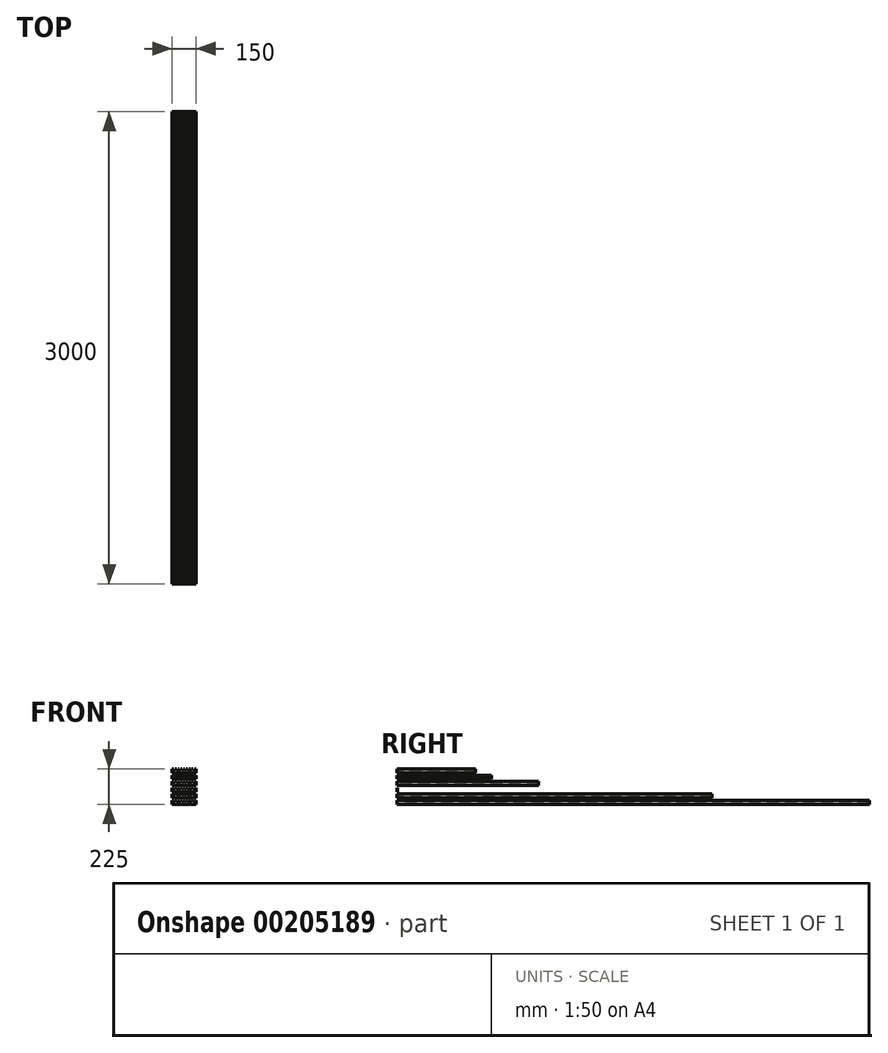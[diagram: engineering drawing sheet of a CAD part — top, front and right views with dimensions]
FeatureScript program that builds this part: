
annotation { "Feature Type Name" : "Feature", "Feature Type Description" : "" }
export const myFeature = defineFeature(function(context is Context, id is Id, definition is map)
    precondition{}
    {
        {
            var Q0;
            Q0=qCreatedBy(makeId("Front.planeOp"),FACE);
            var sketch = newSketch(context, id + "F0", { "sketchPlane" : qUnion([Q0])});
            skLineSegment(sketch, "E0.bottom", {"start": v(0, 0) * mm, "end": v(-150, 0) * mm});
            skLineSegment(sketch, "E0.top", {"start": v(0, 25) * mm, "end": v(-8.82, 25) * mm});
            skLineSegment(sketch, "E0.left", {"start": v(0, 0) * mm, "end": v(0, 25) * mm});
            skLineSegment(sketch, "E0.right", {"start": v(-150, 0) * mm, "end": v(-150, 25) * mm});
            skLineSegment(sketch, "E1", {"start": v(-141.18, 25) * mm, "end": v(-150, 25) * mm});
            skLineSegment(sketch, "E2", {"start": v(-132.35, 25) * mm, "end": v(-141.18, 25) * mm});
            skLineSegment(sketch, "E3", {"start": v(-123.53, 25) * mm, "end": v(-132.35, 25) * mm});
            skLineSegment(sketch, "E4", {"start": v(-114.7, 25) * mm, "end": v(-123.53, 25) * mm});
            skLineSegment(sketch, "E5", {"start": v(-105.88, 25) * mm, "end": v(-114.7, 25) * mm});
            skLineSegment(sketch, "E6", {"start": v(-97.06, 25) * mm, "end": v(-105.88, 25) * mm});
            skLineSegment(sketch, "E7", {"start": v(-88.24, 25) * mm, "end": v(-97.06, 25) * mm});
            skLineSegment(sketch, "E8", {"start": v(-79.41, 25) * mm, "end": v(-88.24, 25) * mm});
            skLineSegment(sketch, "E9", {"start": v(-70.59, 25) * mm, "end": v(-79.41, 25) * mm});
            skLineSegment(sketch, "E10", {"start": v(-61.76, 25) * mm, "end": v(-70.59, 25) * mm});
            skLineSegment(sketch, "E11", {"start": v(-52.94, 25) * mm, "end": v(-61.76, 25) * mm});
            skLineSegment(sketch, "E12", {"start": v(-44.12, 25) * mm, "end": v(-52.94, 25) * mm});
            skLineSegment(sketch, "E13", {"start": v(-35.3, 25) * mm, "end": v(-44.12, 25) * mm});
            skLineSegment(sketch, "E14", {"start": v(-26.47, 25) * mm, "end": v(-35.3, 25) * mm});
            skLineSegment(sketch, "E15", {"start": v(-17.65, 25) * mm, "end": v(-26.47, 25) * mm});
            skLineSegment(sketch, "E16", {"start": v(-8.82, 25) * mm, "end": v(-17.65, 25) * mm});
            skLineSegment(sketch, "E17.bottom", {"start": v(-141.18, 25) * mm, "end": v(-132.35, 25) * mm});
            skLineSegment(sketch, "E17.top", {"start": v(-141.18, 16.18) * mm, "end": v(-132.35, 16.18) * mm});
            skLineSegment(sketch, "E17.left", {"start": v(-141.18, 25) * mm, "end": v(-141.18, 16.18) * mm});
            skLineSegment(sketch, "E17.right", {"start": v(-132.35, 25) * mm, "end": v(-132.35, 16.18) * mm});
            skLineSegment(sketch, "E18.bottom", {"start": v(-123.53, 25) * mm, "end": v(-114.7, 25) * mm});
            skLineSegment(sketch, "E18.top", {"start": v(-123.53, 16.18) * mm, "end": v(-114.7, 16.18) * mm});
            skLineSegment(sketch, "E18.left", {"start": v(-123.53, 25) * mm, "end": v(-123.53, 16.18) * mm});
            skLineSegment(sketch, "E18.right", {"start": v(-114.7, 25) * mm, "end": v(-114.7, 16.18) * mm});
            skLineSegment(sketch, "E19.bottom", {"start": v(-105.88, 25) * mm, "end": v(-97.06, 25) * mm});
            skLineSegment(sketch, "E19.top", {"start": v(-105.88, 16.18) * mm, "end": v(-97.06, 16.18) * mm});
            skLineSegment(sketch, "E19.left", {"start": v(-105.88, 25) * mm, "end": v(-105.88, 16.18) * mm});
            skLineSegment(sketch, "E19.right", {"start": v(-97.06, 25) * mm, "end": v(-97.06, 16.18) * mm});
            skLineSegment(sketch, "E20.bottom", {"start": v(-88.24, 25) * mm, "end": v(-79.41, 25) * mm});
            skLineSegment(sketch, "E20.top", {"start": v(-88.24, 16.18) * mm, "end": v(-79.41, 16.18) * mm});
            skLineSegment(sketch, "E20.left", {"start": v(-88.24, 25) * mm, "end": v(-88.24, 16.18) * mm});
            skLineSegment(sketch, "E20.right", {"start": v(-79.41, 25) * mm, "end": v(-79.41, 16.18) * mm});
            skLineSegment(sketch, "E21.bottom", {"start": v(-70.59, 25) * mm, "end": v(-61.76, 25) * mm});
            skLineSegment(sketch, "E21.top", {"start": v(-70.59, 16.18) * mm, "end": v(-61.76, 16.18) * mm});
            skLineSegment(sketch, "E21.left", {"start": v(-70.59, 25) * mm, "end": v(-70.59, 16.18) * mm});
            skLineSegment(sketch, "E21.right", {"start": v(-61.76, 25) * mm, "end": v(-61.76, 16.18) * mm});
            skLineSegment(sketch, "E22.bottom", {"start": v(-52.94, 25) * mm, "end": v(-44.12, 25) * mm});
            skLineSegment(sketch, "E22.top", {"start": v(-52.94, 16.18) * mm, "end": v(-44.12, 16.18) * mm});
            skLineSegment(sketch, "E22.left", {"start": v(-52.94, 25) * mm, "end": v(-52.94, 16.18) * mm});
            skLineSegment(sketch, "E22.right", {"start": v(-44.12, 25) * mm, "end": v(-44.12, 16.18) * mm});
            skLineSegment(sketch, "E23.bottom", {"start": v(-35.3, 25) * mm, "end": v(-26.47, 25) * mm});
            skLineSegment(sketch, "E23.top", {"start": v(-35.3, 16.18) * mm, "end": v(-26.47, 16.18) * mm});
            skLineSegment(sketch, "E23.left", {"start": v(-35.3, 25) * mm, "end": v(-35.3, 16.18) * mm});
            skLineSegment(sketch, "E23.right", {"start": v(-26.47, 25) * mm, "end": v(-26.47, 16.18) * mm});
            skLineSegment(sketch, "E24.bottom", {"start": v(-17.65, 25) * mm, "end": v(-8.82, 25) * mm});
            skLineSegment(sketch, "E24.top", {"start": v(-17.65, 16.18) * mm, "end": v(-8.82, 16.18) * mm});
            skLineSegment(sketch, "E24.left", {"start": v(-17.65, 25) * mm, "end": v(-17.65, 16.18) * mm});
            skLineSegment(sketch, "E24.right", {"start": v(-8.82, 25) * mm, "end": v(-8.82, 16.18) * mm});
            skLineSegment(sketch, "E25.bottom", {"start": v(-114.7, 0) * mm, "end": v(-110.7, 0) * mm});
            skLineSegment(sketch, "E25.top", {"start": v(-114.7, 4) * mm, "end": v(-110.7, 4) * mm});
            skLineSegment(sketch, "E25.left", {"start": v(-114.7, 0) * mm, "end": v(-114.7, 4) * mm});
            skLineSegment(sketch, "E25.right", {"start": v(-110.7, 0) * mm, "end": v(-110.7, 4) * mm});
            skLineSegment(sketch, "E26.bottom", {"start": v(-35.3, 0) * mm, "end": v(-39.3, 0) * mm});
            skLineSegment(sketch, "E26.top", {"start": v(-35.3, 4) * mm, "end": v(-39.3, 4) * mm});
            skLineSegment(sketch, "E26.left", {"start": v(-35.3, 0) * mm, "end": v(-35.3, 4) * mm});
            skLineSegment(sketch, "E26.right", {"start": v(-39.3, 0) * mm, "end": v(-39.3, 4) * mm});
            skLineSegment(sketch, "E27.0.1.0", {"start": v(-35.3, 65) * mm, "end": v(-44.12, 65) * mm});
            skLineSegment(sketch, "E27.0.1.1", {"start": v(-17.65, 56.18) * mm, "end": v(-8.82, 56.18) * mm});
            skLineSegment(sketch, "E27.0.1.2", {"start": v(-17.65, 65) * mm, "end": v(-17.65, 56.18) * mm});
            skLineSegment(sketch, "E27.0.1.3", {"start": v(-123.53, 65) * mm, "end": v(-114.7, 65) * mm});
            skLineSegment(sketch, "E27.0.1.4", {"start": v(-132.35, 65) * mm, "end": v(-132.35, 56.18) * mm});
            skLineSegment(sketch, "E27.0.1.5", {"start": v(-150, 40) * mm, "end": v(-150, 65) * mm});
            skLineSegment(sketch, "E27.0.1.6", {"start": v(0, 40) * mm, "end": v(0, 65) * mm});
            skLineSegment(sketch, "E27.0.1.7", {"start": v(-17.65, 65) * mm, "end": v(-8.82, 65) * mm});
            skLineSegment(sketch, "E27.0.1.8", {"start": v(-88.24, 65) * mm, "end": v(-97.06, 65) * mm});
            skLineSegment(sketch, "E27.0.1.9", {"start": v(-141.18, 65) * mm, "end": v(-150, 65) * mm});
            skLineSegment(sketch, "E27.0.1.10", {"start": v(-123.53, 56.18) * mm, "end": v(-114.7, 56.18) * mm});
            skLineSegment(sketch, "E27.0.1.11", {"start": v(0, 40) * mm, "end": v(-150, 40) * mm});
            skLineSegment(sketch, "E27.0.1.12", {"start": v(-61.76, 65) * mm, "end": v(-61.76, 56.18) * mm});
            skLineSegment(sketch, "E27.0.1.13", {"start": v(-88.24, 65) * mm, "end": v(-88.24, 56.18) * mm});
            skLineSegment(sketch, "E27.0.1.14", {"start": v(-61.76, 65) * mm, "end": v(-70.59, 65) * mm});
            skLineSegment(sketch, "E27.0.1.15", {"start": v(-70.59, 65) * mm, "end": v(-70.59, 56.18) * mm});
            skLineSegment(sketch, "E27.0.1.16", {"start": v(-97.06, 65) * mm, "end": v(-97.06, 56.18) * mm});
            skLineSegment(sketch, "E27.0.1.17", {"start": v(-26.47, 65) * mm, "end": v(-26.47, 56.18) * mm});
            skLineSegment(sketch, "E27.0.1.18", {"start": v(-141.18, 65) * mm, "end": v(-141.18, 56.18) * mm});
            skLineSegment(sketch, "E27.0.1.19", {"start": v(-105.88, 65) * mm, "end": v(-105.88, 56.18) * mm});
            skLineSegment(sketch, "E27.0.1.20", {"start": v(-70.59, 56.18) * mm, "end": v(-61.76, 56.18) * mm});
            skLineSegment(sketch, "E27.0.1.21", {"start": v(-35.3, 65) * mm, "end": v(-35.3, 56.18) * mm});
            skLineSegment(sketch, "E27.0.1.22", {"start": v(-114.7, 65) * mm, "end": v(-114.7, 56.18) * mm});
            skLineSegment(sketch, "E27.0.1.23", {"start": v(-44.12, 65) * mm, "end": v(-44.12, 56.18) * mm});
            skLineSegment(sketch, "E27.0.1.24", {"start": v(-79.41, 65) * mm, "end": v(-79.41, 56.18) * mm});
            skLineSegment(sketch, "E27.0.1.25", {"start": v(-8.82, 65) * mm, "end": v(-8.82, 56.18) * mm});
            skLineSegment(sketch, "E27.0.1.26", {"start": v(-123.53, 65) * mm, "end": v(-123.53, 56.18) * mm});
            skLineSegment(sketch, "E27.0.1.27", {"start": v(-52.94, 65) * mm, "end": v(-52.94, 56.18) * mm});
            skLineSegment(sketch, "E27.0.1.28", {"start": v(-114.7, 65) * mm, "end": v(-123.53, 65) * mm});
            skLineSegment(sketch, "E27.0.1.29", {"start": v(-70.59, 65) * mm, "end": v(-61.76, 65) * mm});
            skLineSegment(sketch, "E27.0.1.30", {"start": v(-8.82, 65) * mm, "end": v(-17.65, 65) * mm});
            skLineSegment(sketch, "E27.0.1.31", {"start": v(-88.24, 56.18) * mm, "end": v(-79.41, 56.18) * mm});
            skLineSegment(sketch, "E27.0.1.32", {"start": v(-35.3, 40) * mm, "end": v(-39.3, 40) * mm});
            skLineSegment(sketch, "E27.0.1.33", {"start": v(0, 65) * mm, "end": v(-8.82, 65) * mm});
            skLineSegment(sketch, "E27.0.1.34", {"start": v(-35.3, 44) * mm, "end": v(-39.3, 44) * mm});
            skLineSegment(sketch, "E27.0.1.35", {"start": v(-52.94, 56.18) * mm, "end": v(-44.12, 56.18) * mm});
            skLineSegment(sketch, "E27.0.1.36", {"start": v(-110.7, 40) * mm, "end": v(-110.7, 44) * mm});
            skLineSegment(sketch, "E27.0.1.37", {"start": v(-114.7, 40) * mm, "end": v(-114.7, 44) * mm});
            skLineSegment(sketch, "E27.0.1.38", {"start": v(-114.7, 44) * mm, "end": v(-110.7, 44) * mm});
            skLineSegment(sketch, "E27.0.1.39", {"start": v(-141.18, 56.18) * mm, "end": v(-132.35, 56.18) * mm});
            skLineSegment(sketch, "E27.0.1.40", {"start": v(-105.88, 56.18) * mm, "end": v(-97.06, 56.18) * mm});
            skLineSegment(sketch, "E27.0.1.41", {"start": v(-114.7, 40) * mm, "end": v(-110.7, 40) * mm});
            skLineSegment(sketch, "E27.0.1.42", {"start": v(-35.3, 56.18) * mm, "end": v(-26.47, 56.18) * mm});
            skLineSegment(sketch, "E27.0.1.43", {"start": v(-39.3, 40) * mm, "end": v(-39.3, 44) * mm});
            skLineSegment(sketch, "E27.0.1.44", {"start": v(-35.3, 40) * mm, "end": v(-35.3, 44) * mm});
            skLineSegment(sketch, "E27.0.1.45", {"start": v(-105.88, 65) * mm, "end": v(-114.7, 65) * mm});
            skLineSegment(sketch, "E27.0.1.46", {"start": v(-123.53, 65) * mm, "end": v(-132.35, 65) * mm});
            skLineSegment(sketch, "E27.0.1.47", {"start": v(-26.47, 65) * mm, "end": v(-35.3, 65) * mm});
            skLineSegment(sketch, "E27.0.1.48", {"start": v(-88.24, 65) * mm, "end": v(-79.41, 65) * mm});
            skLineSegment(sketch, "E27.0.1.49", {"start": v(-52.94, 65) * mm, "end": v(-44.12, 65) * mm});
            skLineSegment(sketch, "E27.0.1.50", {"start": v(-17.65, 65) * mm, "end": v(-26.47, 65) * mm});
            skLineSegment(sketch, "E27.0.1.51", {"start": v(-132.35, 65) * mm, "end": v(-141.18, 65) * mm});
            skLineSegment(sketch, "E27.0.1.52", {"start": v(-97.06, 65) * mm, "end": v(-105.88, 65) * mm});
            skLineSegment(sketch, "E27.0.1.53", {"start": v(-70.59, 65) * mm, "end": v(-79.41, 65) * mm});
            skLineSegment(sketch, "E27.0.1.54", {"start": v(-52.94, 65) * mm, "end": v(-61.76, 65) * mm});
            skLineSegment(sketch, "E27.0.1.55", {"start": v(-79.41, 65) * mm, "end": v(-88.24, 65) * mm});
            skLineSegment(sketch, "E27.0.1.56", {"start": v(-44.12, 65) * mm, "end": v(-52.94, 65) * mm});
            skLineSegment(sketch, "E27.0.1.57", {"start": v(-105.88, 65) * mm, "end": v(-97.06, 65) * mm});
            skLineSegment(sketch, "E27.0.1.58", {"start": v(-35.3, 65) * mm, "end": v(-26.47, 65) * mm});
            skLineSegment(sketch, "E27.0.1.59", {"start": v(-141.18, 65) * mm, "end": v(-132.35, 65) * mm});
            skLineSegment(sketch, "E27.0.2.0", {"start": v(-35.3, 105) * mm, "end": v(-44.12, 105) * mm});
            skLineSegment(sketch, "E27.0.2.1", {"start": v(-17.65, 96.18) * mm, "end": v(-8.82, 96.18) * mm});
            skLineSegment(sketch, "E27.0.2.2", {"start": v(-17.65, 105) * mm, "end": v(-17.65, 96.18) * mm});
            skLineSegment(sketch, "E27.0.2.3", {"start": v(-123.53, 105) * mm, "end": v(-114.7, 105) * mm});
            skLineSegment(sketch, "E27.0.2.4", {"start": v(-132.35, 105) * mm, "end": v(-132.35, 96.18) * mm});
            skLineSegment(sketch, "E27.0.2.5", {"start": v(-150, 80) * mm, "end": v(-150, 105) * mm});
            skLineSegment(sketch, "E27.0.2.6", {"start": v(0, 80) * mm, "end": v(0, 105) * mm});
            skLineSegment(sketch, "E27.0.2.7", {"start": v(-17.65, 105) * mm, "end": v(-8.82, 105) * mm});
            skLineSegment(sketch, "E27.0.2.8", {"start": v(-88.24, 105) * mm, "end": v(-97.06, 105) * mm});
            skLineSegment(sketch, "E27.0.2.9", {"start": v(-141.18, 105) * mm, "end": v(-150, 105) * mm});
            skLineSegment(sketch, "E27.0.2.10", {"start": v(-123.53, 96.18) * mm, "end": v(-114.7, 96.18) * mm});
            skLineSegment(sketch, "E27.0.2.11", {"start": v(0, 80) * mm, "end": v(-150, 80) * mm});
            skLineSegment(sketch, "E27.0.2.12", {"start": v(-61.76, 105) * mm, "end": v(-61.76, 96.18) * mm});
            skLineSegment(sketch, "E27.0.2.13", {"start": v(-88.24, 105) * mm, "end": v(-88.24, 96.18) * mm});
            skLineSegment(sketch, "E27.0.2.14", {"start": v(-61.76, 105) * mm, "end": v(-70.59, 105) * mm});
            skLineSegment(sketch, "E27.0.2.15", {"start": v(-70.59, 105) * mm, "end": v(-70.59, 96.18) * mm});
            skLineSegment(sketch, "E27.0.2.16", {"start": v(-97.06, 105) * mm, "end": v(-97.06, 96.18) * mm});
            skLineSegment(sketch, "E27.0.2.17", {"start": v(-26.47, 105) * mm, "end": v(-26.47, 96.18) * mm});
            skLineSegment(sketch, "E27.0.2.18", {"start": v(-141.18, 105) * mm, "end": v(-141.18, 96.18) * mm});
            skLineSegment(sketch, "E27.0.2.19", {"start": v(-105.88, 105) * mm, "end": v(-105.88, 96.18) * mm});
            skLineSegment(sketch, "E27.0.2.20", {"start": v(-70.59, 96.18) * mm, "end": v(-61.76, 96.18) * mm});
            skLineSegment(sketch, "E27.0.2.21", {"start": v(-35.3, 105) * mm, "end": v(-35.3, 96.18) * mm});
            skLineSegment(sketch, "E27.0.2.22", {"start": v(-114.7, 105) * mm, "end": v(-114.7, 96.18) * mm});
            skLineSegment(sketch, "E27.0.2.23", {"start": v(-44.12, 105) * mm, "end": v(-44.12, 96.18) * mm});
            skLineSegment(sketch, "E27.0.2.24", {"start": v(-79.41, 105) * mm, "end": v(-79.41, 96.18) * mm});
            skLineSegment(sketch, "E27.0.2.25", {"start": v(-8.82, 105) * mm, "end": v(-8.82, 96.18) * mm});
            skLineSegment(sketch, "E27.0.2.26", {"start": v(-123.53, 105) * mm, "end": v(-123.53, 96.18) * mm});
            skLineSegment(sketch, "E27.0.2.27", {"start": v(-52.94, 105) * mm, "end": v(-52.94, 96.18) * mm});
            skLineSegment(sketch, "E27.0.2.28", {"start": v(-114.7, 105) * mm, "end": v(-123.53, 105) * mm});
            skLineSegment(sketch, "E27.0.2.29", {"start": v(-70.59, 105) * mm, "end": v(-61.76, 105) * mm});
            skLineSegment(sketch, "E27.0.2.30", {"start": v(-8.82, 105) * mm, "end": v(-17.65, 105) * mm});
            skLineSegment(sketch, "E27.0.2.31", {"start": v(-88.24, 96.18) * mm, "end": v(-79.41, 96.18) * mm});
            skLineSegment(sketch, "E27.0.2.32", {"start": v(-35.3, 80) * mm, "end": v(-39.3, 80) * mm});
            skLineSegment(sketch, "E27.0.2.33", {"start": v(0, 105) * mm, "end": v(-8.82, 105) * mm});
            skLineSegment(sketch, "E27.0.2.34", {"start": v(-35.3, 84) * mm, "end": v(-39.3, 84) * mm});
            skLineSegment(sketch, "E27.0.2.35", {"start": v(-52.94, 96.18) * mm, "end": v(-44.12, 96.18) * mm});
            skLineSegment(sketch, "E27.0.2.36", {"start": v(-110.7, 80) * mm, "end": v(-110.7, 84) * mm});
            skLineSegment(sketch, "E27.0.2.37", {"start": v(-114.7, 80) * mm, "end": v(-114.7, 84) * mm});
            skLineSegment(sketch, "E27.0.2.38", {"start": v(-114.7, 84) * mm, "end": v(-110.7, 84) * mm});
            skLineSegment(sketch, "E27.0.2.39", {"start": v(-141.18, 96.18) * mm, "end": v(-132.35, 96.18) * mm});
            skLineSegment(sketch, "E27.0.2.40", {"start": v(-105.88, 96.18) * mm, "end": v(-97.06, 96.18) * mm});
            skLineSegment(sketch, "E27.0.2.41", {"start": v(-114.7, 80) * mm, "end": v(-110.7, 80) * mm});
            skLineSegment(sketch, "E27.0.2.42", {"start": v(-35.3, 96.18) * mm, "end": v(-26.47, 96.18) * mm});
            skLineSegment(sketch, "E27.0.2.43", {"start": v(-39.3, 80) * mm, "end": v(-39.3, 84) * mm});
            skLineSegment(sketch, "E27.0.2.44", {"start": v(-35.3, 80) * mm, "end": v(-35.3, 84) * mm});
            skLineSegment(sketch, "E27.0.2.45", {"start": v(-105.88, 105) * mm, "end": v(-114.7, 105) * mm});
            skLineSegment(sketch, "E27.0.2.46", {"start": v(-123.53, 105) * mm, "end": v(-132.35, 105) * mm});
            skLineSegment(sketch, "E27.0.2.47", {"start": v(-26.47, 105) * mm, "end": v(-35.3, 105) * mm});
            skLineSegment(sketch, "E27.0.2.48", {"start": v(-88.24, 105) * mm, "end": v(-79.41, 105) * mm});
            skLineSegment(sketch, "E27.0.2.49", {"start": v(-52.94, 105) * mm, "end": v(-44.12, 105) * mm});
            skLineSegment(sketch, "E27.0.2.50", {"start": v(-17.65, 105) * mm, "end": v(-26.47, 105) * mm});
            skLineSegment(sketch, "E27.0.2.51", {"start": v(-132.35, 105) * mm, "end": v(-141.18, 105) * mm});
            skLineSegment(sketch, "E27.0.2.52", {"start": v(-97.06, 105) * mm, "end": v(-105.88, 105) * mm});
            skLineSegment(sketch, "E27.0.2.53", {"start": v(-70.59, 105) * mm, "end": v(-79.41, 105) * mm});
            skLineSegment(sketch, "E27.0.2.54", {"start": v(-52.94, 105) * mm, "end": v(-61.76, 105) * mm});
            skLineSegment(sketch, "E27.0.2.55", {"start": v(-79.41, 105) * mm, "end": v(-88.24, 105) * mm});
            skLineSegment(sketch, "E27.0.2.56", {"start": v(-44.12, 105) * mm, "end": v(-52.94, 105) * mm});
            skLineSegment(sketch, "E27.0.2.57", {"start": v(-105.88, 105) * mm, "end": v(-97.06, 105) * mm});
            skLineSegment(sketch, "E27.0.2.58", {"start": v(-35.3, 105) * mm, "end": v(-26.47, 105) * mm});
            skLineSegment(sketch, "E27.0.2.59", {"start": v(-141.18, 105) * mm, "end": v(-132.35, 105) * mm});
            skLineSegment(sketch, "E27.0.3.0", {"start": v(-35.3, 145) * mm, "end": v(-44.12, 145) * mm});
            skLineSegment(sketch, "E27.0.3.1", {"start": v(-17.65, 136.18) * mm, "end": v(-8.82, 136.18) * mm});
            skLineSegment(sketch, "E27.0.3.2", {"start": v(-17.65, 145) * mm, "end": v(-17.65, 136.18) * mm});
            skLineSegment(sketch, "E27.0.3.3", {"start": v(-123.53, 145) * mm, "end": v(-114.7, 145) * mm});
            skLineSegment(sketch, "E27.0.3.4", {"start": v(-132.35, 145) * mm, "end": v(-132.35, 136.18) * mm});
            skLineSegment(sketch, "E27.0.3.5", {"start": v(-150, 120) * mm, "end": v(-150, 145) * mm});
            skLineSegment(sketch, "E27.0.3.6", {"start": v(0, 120) * mm, "end": v(0, 145) * mm});
            skLineSegment(sketch, "E27.0.3.7", {"start": v(-17.65, 145) * mm, "end": v(-8.82, 145) * mm});
            skLineSegment(sketch, "E27.0.3.8", {"start": v(-88.24, 145) * mm, "end": v(-97.06, 145) * mm});
            skLineSegment(sketch, "E27.0.3.9", {"start": v(-141.18, 145) * mm, "end": v(-150, 145) * mm});
            skLineSegment(sketch, "E27.0.3.10", {"start": v(-123.53, 136.18) * mm, "end": v(-114.7, 136.18) * mm});
            skLineSegment(sketch, "E27.0.3.11", {"start": v(0, 120) * mm, "end": v(-150, 120) * mm});
            skLineSegment(sketch, "E27.0.3.12", {"start": v(-61.76, 145) * mm, "end": v(-61.76, 136.18) * mm});
            skLineSegment(sketch, "E27.0.3.13", {"start": v(-88.24, 145) * mm, "end": v(-88.24, 136.18) * mm});
            skLineSegment(sketch, "E27.0.3.14", {"start": v(-61.76, 145) * mm, "end": v(-70.59, 145) * mm});
            skLineSegment(sketch, "E27.0.3.15", {"start": v(-70.59, 145) * mm, "end": v(-70.59, 136.18) * mm});
            skLineSegment(sketch, "E27.0.3.16", {"start": v(-97.06, 145) * mm, "end": v(-97.06, 136.18) * mm});
            skLineSegment(sketch, "E27.0.3.17", {"start": v(-26.47, 145) * mm, "end": v(-26.47, 136.18) * mm});
            skLineSegment(sketch, "E27.0.3.18", {"start": v(-141.18, 145) * mm, "end": v(-141.18, 136.18) * mm});
            skLineSegment(sketch, "E27.0.3.19", {"start": v(-105.88, 145) * mm, "end": v(-105.88, 136.18) * mm});
            skLineSegment(sketch, "E27.0.3.20", {"start": v(-70.59, 136.18) * mm, "end": v(-61.76, 136.18) * mm});
            skLineSegment(sketch, "E27.0.3.21", {"start": v(-35.3, 145) * mm, "end": v(-35.3, 136.18) * mm});
            skLineSegment(sketch, "E27.0.3.22", {"start": v(-114.7, 145) * mm, "end": v(-114.7, 136.18) * mm});
            skLineSegment(sketch, "E27.0.3.23", {"start": v(-44.12, 145) * mm, "end": v(-44.12, 136.18) * mm});
            skLineSegment(sketch, "E27.0.3.24", {"start": v(-79.41, 145) * mm, "end": v(-79.41, 136.18) * mm});
            skLineSegment(sketch, "E27.0.3.25", {"start": v(-8.82, 145) * mm, "end": v(-8.82, 136.18) * mm});
            skLineSegment(sketch, "E27.0.3.26", {"start": v(-123.53, 145) * mm, "end": v(-123.53, 136.18) * mm});
            skLineSegment(sketch, "E27.0.3.27", {"start": v(-52.94, 145) * mm, "end": v(-52.94, 136.18) * mm});
            skLineSegment(sketch, "E27.0.3.28", {"start": v(-114.7, 145) * mm, "end": v(-123.53, 145) * mm});
            skLineSegment(sketch, "E27.0.3.29", {"start": v(-70.59, 145) * mm, "end": v(-61.76, 145) * mm});
            skLineSegment(sketch, "E27.0.3.30", {"start": v(-8.82, 145) * mm, "end": v(-17.65, 145) * mm});
            skLineSegment(sketch, "E27.0.3.31", {"start": v(-88.24, 136.18) * mm, "end": v(-79.41, 136.18) * mm});
            skLineSegment(sketch, "E27.0.3.32", {"start": v(-35.3, 120) * mm, "end": v(-39.3, 120) * mm});
            skLineSegment(sketch, "E27.0.3.33", {"start": v(0, 145) * mm, "end": v(-8.82, 145) * mm});
            skLineSegment(sketch, "E27.0.3.34", {"start": v(-35.3, 124) * mm, "end": v(-39.3, 124) * mm});
            skLineSegment(sketch, "E27.0.3.35", {"start": v(-52.94, 136.18) * mm, "end": v(-44.12, 136.18) * mm});
            skLineSegment(sketch, "E27.0.3.36", {"start": v(-110.7, 120) * mm, "end": v(-110.7, 124) * mm});
            skLineSegment(sketch, "E27.0.3.37", {"start": v(-114.7, 120) * mm, "end": v(-114.7, 124) * mm});
            skLineSegment(sketch, "E27.0.3.38", {"start": v(-114.7, 124) * mm, "end": v(-110.7, 124) * mm});
            skLineSegment(sketch, "E27.0.3.39", {"start": v(-141.18, 136.18) * mm, "end": v(-132.35, 136.18) * mm});
            skLineSegment(sketch, "E27.0.3.40", {"start": v(-105.88, 136.18) * mm, "end": v(-97.06, 136.18) * mm});
            skLineSegment(sketch, "E27.0.3.41", {"start": v(-114.7, 120) * mm, "end": v(-110.7, 120) * mm});
            skLineSegment(sketch, "E27.0.3.42", {"start": v(-35.3, 136.18) * mm, "end": v(-26.47, 136.18) * mm});
            skLineSegment(sketch, "E27.0.3.43", {"start": v(-39.3, 120) * mm, "end": v(-39.3, 124) * mm});
            skLineSegment(sketch, "E27.0.3.44", {"start": v(-35.3, 120) * mm, "end": v(-35.3, 124) * mm});
            skLineSegment(sketch, "E27.0.3.45", {"start": v(-105.88, 145) * mm, "end": v(-114.7, 145) * mm});
            skLineSegment(sketch, "E27.0.3.46", {"start": v(-123.53, 145) * mm, "end": v(-132.35, 145) * mm});
            skLineSegment(sketch, "E27.0.3.47", {"start": v(-26.47, 145) * mm, "end": v(-35.3, 145) * mm});
            skLineSegment(sketch, "E27.0.3.48", {"start": v(-88.24, 145) * mm, "end": v(-79.41, 145) * mm});
            skLineSegment(sketch, "E27.0.3.49", {"start": v(-52.94, 145) * mm, "end": v(-44.12, 145) * mm});
            skLineSegment(sketch, "E27.0.3.50", {"start": v(-17.65, 145) * mm, "end": v(-26.47, 145) * mm});
            skLineSegment(sketch, "E27.0.3.51", {"start": v(-132.35, 145) * mm, "end": v(-141.18, 145) * mm});
            skLineSegment(sketch, "E27.0.3.52", {"start": v(-97.06, 145) * mm, "end": v(-105.88, 145) * mm});
            skLineSegment(sketch, "E27.0.3.53", {"start": v(-70.59, 145) * mm, "end": v(-79.41, 145) * mm});
            skLineSegment(sketch, "E27.0.3.54", {"start": v(-52.94, 145) * mm, "end": v(-61.76, 145) * mm});
            skLineSegment(sketch, "E27.0.3.55", {"start": v(-79.41, 145) * mm, "end": v(-88.24, 145) * mm});
            skLineSegment(sketch, "E27.0.3.56", {"start": v(-44.12, 145) * mm, "end": v(-52.94, 145) * mm});
            skLineSegment(sketch, "E27.0.3.57", {"start": v(-105.88, 145) * mm, "end": v(-97.06, 145) * mm});
            skLineSegment(sketch, "E27.0.3.58", {"start": v(-35.3, 145) * mm, "end": v(-26.47, 145) * mm});
            skLineSegment(sketch, "E27.0.3.59", {"start": v(-141.18, 145) * mm, "end": v(-132.35, 145) * mm});
            skLineSegment(sketch, "E27.0.4.0", {"start": v(-35.3, 185) * mm, "end": v(-44.12, 185) * mm});
            skLineSegment(sketch, "E27.0.4.1", {"start": v(-17.65, 176.18) * mm, "end": v(-8.82, 176.18) * mm});
            skLineSegment(sketch, "E27.0.4.2", {"start": v(-17.65, 185) * mm, "end": v(-17.65, 176.18) * mm});
            skLineSegment(sketch, "E27.0.4.3", {"start": v(-123.53, 185) * mm, "end": v(-114.7, 185) * mm});
            skLineSegment(sketch, "E27.0.4.4", {"start": v(-132.35, 185) * mm, "end": v(-132.35, 176.18) * mm});
            skLineSegment(sketch, "E27.0.4.5", {"start": v(-150, 160) * mm, "end": v(-150, 185) * mm});
            skLineSegment(sketch, "E27.0.4.6", {"start": v(0, 160) * mm, "end": v(0, 185) * mm});
            skLineSegment(sketch, "E27.0.4.7", {"start": v(-17.65, 185) * mm, "end": v(-8.82, 185) * mm});
            skLineSegment(sketch, "E27.0.4.8", {"start": v(-88.24, 185) * mm, "end": v(-97.06, 185) * mm});
            skLineSegment(sketch, "E27.0.4.9", {"start": v(-141.18, 185) * mm, "end": v(-150, 185) * mm});
            skLineSegment(sketch, "E27.0.4.10", {"start": v(-123.53, 176.18) * mm, "end": v(-114.7, 176.18) * mm});
            skLineSegment(sketch, "E27.0.4.11", {"start": v(0, 160) * mm, "end": v(-150, 160) * mm});
            skLineSegment(sketch, "E27.0.4.12", {"start": v(-61.76, 185) * mm, "end": v(-61.76, 176.18) * mm});
            skLineSegment(sketch, "E27.0.4.13", {"start": v(-88.24, 185) * mm, "end": v(-88.24, 176.18) * mm});
            skLineSegment(sketch, "E27.0.4.14", {"start": v(-61.76, 185) * mm, "end": v(-70.59, 185) * mm});
            skLineSegment(sketch, "E27.0.4.15", {"start": v(-70.59, 185) * mm, "end": v(-70.59, 176.18) * mm});
            skLineSegment(sketch, "E27.0.4.16", {"start": v(-97.06, 185) * mm, "end": v(-97.06, 176.18) * mm});
            skLineSegment(sketch, "E27.0.4.17", {"start": v(-26.47, 185) * mm, "end": v(-26.47, 176.18) * mm});
            skLineSegment(sketch, "E27.0.4.18", {"start": v(-141.18, 185) * mm, "end": v(-141.18, 176.18) * mm});
            skLineSegment(sketch, "E27.0.4.19", {"start": v(-105.88, 185) * mm, "end": v(-105.88, 176.18) * mm});
            skLineSegment(sketch, "E27.0.4.20", {"start": v(-70.59, 176.18) * mm, "end": v(-61.76, 176.18) * mm});
            skLineSegment(sketch, "E27.0.4.21", {"start": v(-35.3, 185) * mm, "end": v(-35.3, 176.18) * mm});
            skLineSegment(sketch, "E27.0.4.22", {"start": v(-114.7, 185) * mm, "end": v(-114.7, 176.18) * mm});
            skLineSegment(sketch, "E27.0.4.23", {"start": v(-44.12, 185) * mm, "end": v(-44.12, 176.18) * mm});
            skLineSegment(sketch, "E27.0.4.24", {"start": v(-79.41, 185) * mm, "end": v(-79.41, 176.18) * mm});
            skLineSegment(sketch, "E27.0.4.25", {"start": v(-8.82, 185) * mm, "end": v(-8.82, 176.18) * mm});
            skLineSegment(sketch, "E27.0.4.26", {"start": v(-123.53, 185) * mm, "end": v(-123.53, 176.18) * mm});
            skLineSegment(sketch, "E27.0.4.27", {"start": v(-52.94, 185) * mm, "end": v(-52.94, 176.18) * mm});
            skLineSegment(sketch, "E27.0.4.28", {"start": v(-114.7, 185) * mm, "end": v(-123.53, 185) * mm});
            skLineSegment(sketch, "E27.0.4.29", {"start": v(-70.59, 185) * mm, "end": v(-61.76, 185) * mm});
            skLineSegment(sketch, "E27.0.4.30", {"start": v(-8.82, 185) * mm, "end": v(-17.65, 185) * mm});
            skLineSegment(sketch, "E27.0.4.31", {"start": v(-88.24, 176.18) * mm, "end": v(-79.41, 176.18) * mm});
            skLineSegment(sketch, "E27.0.4.32", {"start": v(-35.3, 160) * mm, "end": v(-39.3, 160) * mm});
            skLineSegment(sketch, "E27.0.4.33", {"start": v(0, 185) * mm, "end": v(-8.82, 185) * mm});
            skLineSegment(sketch, "E27.0.4.34", {"start": v(-35.3, 164) * mm, "end": v(-39.3, 164) * mm});
            skLineSegment(sketch, "E27.0.4.35", {"start": v(-52.94, 176.18) * mm, "end": v(-44.12, 176.18) * mm});
            skLineSegment(sketch, "E27.0.4.36", {"start": v(-110.7, 160) * mm, "end": v(-110.7, 164) * mm});
            skLineSegment(sketch, "E27.0.4.37", {"start": v(-114.7, 160) * mm, "end": v(-114.7, 164) * mm});
            skLineSegment(sketch, "E27.0.4.38", {"start": v(-114.7, 164) * mm, "end": v(-110.7, 164) * mm});
            skLineSegment(sketch, "E27.0.4.39", {"start": v(-141.18, 176.18) * mm, "end": v(-132.35, 176.18) * mm});
            skLineSegment(sketch, "E27.0.4.40", {"start": v(-105.88, 176.18) * mm, "end": v(-97.06, 176.18) * mm});
            skLineSegment(sketch, "E27.0.4.41", {"start": v(-114.7, 160) * mm, "end": v(-110.7, 160) * mm});
            skLineSegment(sketch, "E27.0.4.42", {"start": v(-35.3, 176.18) * mm, "end": v(-26.47, 176.18) * mm});
            skLineSegment(sketch, "E27.0.4.43", {"start": v(-39.3, 160) * mm, "end": v(-39.3, 164) * mm});
            skLineSegment(sketch, "E27.0.4.44", {"start": v(-35.3, 160) * mm, "end": v(-35.3, 164) * mm});
            skLineSegment(sketch, "E27.0.4.45", {"start": v(-105.88, 185) * mm, "end": v(-114.7, 185) * mm});
            skLineSegment(sketch, "E27.0.4.46", {"start": v(-123.53, 185) * mm, "end": v(-132.35, 185) * mm});
            skLineSegment(sketch, "E27.0.4.47", {"start": v(-26.47, 185) * mm, "end": v(-35.3, 185) * mm});
            skLineSegment(sketch, "E27.0.4.48", {"start": v(-88.24, 185) * mm, "end": v(-79.41, 185) * mm});
            skLineSegment(sketch, "E27.0.4.49", {"start": v(-52.94, 185) * mm, "end": v(-44.12, 185) * mm});
            skLineSegment(sketch, "E27.0.4.50", {"start": v(-17.65, 185) * mm, "end": v(-26.47, 185) * mm});
            skLineSegment(sketch, "E27.0.4.51", {"start": v(-132.35, 185) * mm, "end": v(-141.18, 185) * mm});
            skLineSegment(sketch, "E27.0.4.52", {"start": v(-97.06, 185) * mm, "end": v(-105.88, 185) * mm});
            skLineSegment(sketch, "E27.0.4.53", {"start": v(-70.59, 185) * mm, "end": v(-79.41, 185) * mm});
            skLineSegment(sketch, "E27.0.4.54", {"start": v(-52.94, 185) * mm, "end": v(-61.76, 185) * mm});
            skLineSegment(sketch, "E27.0.4.55", {"start": v(-79.41, 185) * mm, "end": v(-88.24, 185) * mm});
            skLineSegment(sketch, "E27.0.4.56", {"start": v(-44.12, 185) * mm, "end": v(-52.94, 185) * mm});
            skLineSegment(sketch, "E27.0.4.57", {"start": v(-105.88, 185) * mm, "end": v(-97.06, 185) * mm});
            skLineSegment(sketch, "E27.0.4.58", {"start": v(-35.3, 185) * mm, "end": v(-26.47, 185) * mm});
            skLineSegment(sketch, "E27.0.4.59", {"start": v(-141.18, 185) * mm, "end": v(-132.35, 185) * mm});
            skLineSegment(sketch, "E27.0.5.0", {"start": v(-35.3, 225) * mm, "end": v(-44.12, 225) * mm});
            skLineSegment(sketch, "E27.0.5.1", {"start": v(-17.65, 216.18) * mm, "end": v(-8.82, 216.18) * mm});
            skLineSegment(sketch, "E27.0.5.2", {"start": v(-17.65, 225) * mm, "end": v(-17.65, 216.18) * mm});
            skLineSegment(sketch, "E27.0.5.3", {"start": v(-123.53, 225) * mm, "end": v(-114.7, 225) * mm});
            skLineSegment(sketch, "E27.0.5.4", {"start": v(-132.35, 225) * mm, "end": v(-132.35, 216.18) * mm});
            skLineSegment(sketch, "E27.0.5.5", {"start": v(-150, 200) * mm, "end": v(-150, 225) * mm});
            skLineSegment(sketch, "E27.0.5.6", {"start": v(0, 200) * mm, "end": v(0, 225) * mm});
            skLineSegment(sketch, "E27.0.5.7", {"start": v(-17.65, 225) * mm, "end": v(-8.82, 225) * mm});
            skLineSegment(sketch, "E27.0.5.8", {"start": v(-88.24, 225) * mm, "end": v(-97.06, 225) * mm});
            skLineSegment(sketch, "E27.0.5.9", {"start": v(-141.18, 225) * mm, "end": v(-150, 225) * mm});
            skLineSegment(sketch, "E27.0.5.10", {"start": v(-123.53, 216.18) * mm, "end": v(-114.7, 216.18) * mm});
            skLineSegment(sketch, "E27.0.5.11", {"start": v(0, 200) * mm, "end": v(-150, 200) * mm});
            skLineSegment(sketch, "E27.0.5.12", {"start": v(-61.76, 225) * mm, "end": v(-61.76, 216.18) * mm});
            skLineSegment(sketch, "E27.0.5.13", {"start": v(-88.24, 225) * mm, "end": v(-88.24, 216.18) * mm});
            skLineSegment(sketch, "E27.0.5.14", {"start": v(-61.76, 225) * mm, "end": v(-70.59, 225) * mm});
            skLineSegment(sketch, "E27.0.5.15", {"start": v(-70.59, 225) * mm, "end": v(-70.59, 216.18) * mm});
            skLineSegment(sketch, "E27.0.5.16", {"start": v(-97.06, 225) * mm, "end": v(-97.06, 216.18) * mm});
            skLineSegment(sketch, "E27.0.5.17", {"start": v(-26.47, 225) * mm, "end": v(-26.47, 216.18) * mm});
            skLineSegment(sketch, "E27.0.5.18", {"start": v(-141.18, 225) * mm, "end": v(-141.18, 216.18) * mm});
            skLineSegment(sketch, "E27.0.5.19", {"start": v(-105.88, 225) * mm, "end": v(-105.88, 216.18) * mm});
            skLineSegment(sketch, "E27.0.5.20", {"start": v(-70.59, 216.18) * mm, "end": v(-61.76, 216.18) * mm});
            skLineSegment(sketch, "E27.0.5.21", {"start": v(-35.3, 225) * mm, "end": v(-35.3, 216.18) * mm});
            skLineSegment(sketch, "E27.0.5.22", {"start": v(-114.7, 225) * mm, "end": v(-114.7, 216.18) * mm});
            skLineSegment(sketch, "E27.0.5.23", {"start": v(-44.12, 225) * mm, "end": v(-44.12, 216.18) * mm});
            skLineSegment(sketch, "E27.0.5.24", {"start": v(-79.41, 225) * mm, "end": v(-79.41, 216.18) * mm});
            skLineSegment(sketch, "E27.0.5.25", {"start": v(-8.82, 225) * mm, "end": v(-8.82, 216.18) * mm});
            skLineSegment(sketch, "E27.0.5.26", {"start": v(-123.53, 225) * mm, "end": v(-123.53, 216.18) * mm});
            skLineSegment(sketch, "E27.0.5.27", {"start": v(-52.94, 225) * mm, "end": v(-52.94, 216.18) * mm});
            skLineSegment(sketch, "E27.0.5.28", {"start": v(-114.7, 225) * mm, "end": v(-123.53, 225) * mm});
            skLineSegment(sketch, "E27.0.5.29", {"start": v(-70.59, 225) * mm, "end": v(-61.76, 225) * mm});
            skLineSegment(sketch, "E27.0.5.30", {"start": v(-8.82, 225) * mm, "end": v(-17.65, 225) * mm});
            skLineSegment(sketch, "E27.0.5.31", {"start": v(-88.24, 216.18) * mm, "end": v(-79.41, 216.18) * mm});
            skLineSegment(sketch, "E27.0.5.32", {"start": v(-35.3, 200) * mm, "end": v(-39.3, 200) * mm});
            skLineSegment(sketch, "E27.0.5.33", {"start": v(0, 225) * mm, "end": v(-8.82, 225) * mm});
            skLineSegment(sketch, "E27.0.5.34", {"start": v(-35.3, 204) * mm, "end": v(-39.3, 204) * mm});
            skLineSegment(sketch, "E27.0.5.35", {"start": v(-52.94, 216.18) * mm, "end": v(-44.12, 216.18) * mm});
            skLineSegment(sketch, "E27.0.5.36", {"start": v(-110.7, 200) * mm, "end": v(-110.7, 204) * mm});
            skLineSegment(sketch, "E27.0.5.37", {"start": v(-114.7, 200) * mm, "end": v(-114.7, 204) * mm});
            skLineSegment(sketch, "E27.0.5.38", {"start": v(-114.7, 204) * mm, "end": v(-110.7, 204) * mm});
            skLineSegment(sketch, "E27.0.5.39", {"start": v(-141.18, 216.18) * mm, "end": v(-132.35, 216.18) * mm});
            skLineSegment(sketch, "E27.0.5.40", {"start": v(-105.88, 216.18) * mm, "end": v(-97.06, 216.18) * mm});
            skLineSegment(sketch, "E27.0.5.41", {"start": v(-114.7, 200) * mm, "end": v(-110.7, 200) * mm});
            skLineSegment(sketch, "E27.0.5.42", {"start": v(-35.3, 216.18) * mm, "end": v(-26.47, 216.18) * mm});
            skLineSegment(sketch, "E27.0.5.43", {"start": v(-39.3, 200) * mm, "end": v(-39.3, 204) * mm});
            skLineSegment(sketch, "E27.0.5.44", {"start": v(-35.3, 200) * mm, "end": v(-35.3, 204) * mm});
            skLineSegment(sketch, "E27.0.5.45", {"start": v(-105.88, 225) * mm, "end": v(-114.7, 225) * mm});
            skLineSegment(sketch, "E27.0.5.46", {"start": v(-123.53, 225) * mm, "end": v(-132.35, 225) * mm});
            skLineSegment(sketch, "E27.0.5.47", {"start": v(-26.47, 225) * mm, "end": v(-35.3, 225) * mm});
            skLineSegment(sketch, "E27.0.5.48", {"start": v(-88.24, 225) * mm, "end": v(-79.41, 225) * mm});
            skLineSegment(sketch, "E27.0.5.49", {"start": v(-52.94, 225) * mm, "end": v(-44.12, 225) * mm});
            skLineSegment(sketch, "E27.0.5.50", {"start": v(-17.65, 225) * mm, "end": v(-26.47, 225) * mm});
            skLineSegment(sketch, "E27.0.5.51", {"start": v(-132.35, 225) * mm, "end": v(-141.18, 225) * mm});
            skLineSegment(sketch, "E27.0.5.52", {"start": v(-97.06, 225) * mm, "end": v(-105.88, 225) * mm});
            skLineSegment(sketch, "E27.0.5.53", {"start": v(-70.59, 225) * mm, "end": v(-79.41, 225) * mm});
            skLineSegment(sketch, "E27.0.5.54", {"start": v(-52.94, 225) * mm, "end": v(-61.76, 225) * mm});
            skLineSegment(sketch, "E27.0.5.55", {"start": v(-79.41, 225) * mm, "end": v(-88.24, 225) * mm});
            skLineSegment(sketch, "E27.0.5.56", {"start": v(-44.12, 225) * mm, "end": v(-52.94, 225) * mm});
            skLineSegment(sketch, "E27.0.5.57", {"start": v(-105.88, 225) * mm, "end": v(-97.06, 225) * mm});
            skLineSegment(sketch, "E27.0.5.58", {"start": v(-35.3, 225) * mm, "end": v(-26.47, 225) * mm});
            skLineSegment(sketch, "E27.0.5.59", {"start": v(-141.18, 225) * mm, "end": v(-132.35, 225) * mm});
            skLineSegment(sketch, "E27.0.6.0", {"start": v(-35.3, 265) * mm, "end": v(-44.12, 265) * mm});
            skLineSegment(sketch, "E27.0.6.1", {"start": v(-17.65, 256.18) * mm, "end": v(-8.82, 256.18) * mm});
            skLineSegment(sketch, "E27.0.6.2", {"start": v(-17.65, 265) * mm, "end": v(-17.65, 256.18) * mm});
            skLineSegment(sketch, "E27.0.6.3", {"start": v(-123.53, 265) * mm, "end": v(-114.7, 265) * mm});
            skLineSegment(sketch, "E27.0.6.4", {"start": v(-132.35, 265) * mm, "end": v(-132.35, 256.18) * mm});
            skLineSegment(sketch, "E27.0.6.5", {"start": v(-150, 240) * mm, "end": v(-150, 265) * mm});
            skLineSegment(sketch, "E27.0.6.6", {"start": v(0, 240) * mm, "end": v(0, 265) * mm});
            skLineSegment(sketch, "E27.0.6.7", {"start": v(-17.65, 265) * mm, "end": v(-8.82, 265) * mm});
            skLineSegment(sketch, "E27.0.6.8", {"start": v(-88.24, 265) * mm, "end": v(-97.06, 265) * mm});
            skLineSegment(sketch, "E27.0.6.9", {"start": v(-141.18, 265) * mm, "end": v(-150, 265) * mm});
            skLineSegment(sketch, "E27.0.6.10", {"start": v(-123.53, 256.18) * mm, "end": v(-114.7, 256.18) * mm});
            skLineSegment(sketch, "E27.0.6.11", {"start": v(0, 240) * mm, "end": v(-150, 240) * mm});
            skLineSegment(sketch, "E27.0.6.12", {"start": v(-61.76, 265) * mm, "end": v(-61.76, 256.18) * mm});
            skLineSegment(sketch, "E27.0.6.13", {"start": v(-88.24, 265) * mm, "end": v(-88.24, 256.18) * mm});
            skLineSegment(sketch, "E27.0.6.14", {"start": v(-61.76, 265) * mm, "end": v(-70.59, 265) * mm});
            skLineSegment(sketch, "E27.0.6.15", {"start": v(-70.59, 265) * mm, "end": v(-70.59, 256.18) * mm});
            skLineSegment(sketch, "E27.0.6.16", {"start": v(-97.06, 265) * mm, "end": v(-97.06, 256.18) * mm});
            skLineSegment(sketch, "E27.0.6.17", {"start": v(-26.47, 265) * mm, "end": v(-26.47, 256.18) * mm});
            skLineSegment(sketch, "E27.0.6.18", {"start": v(-141.18, 265) * mm, "end": v(-141.18, 256.18) * mm});
            skLineSegment(sketch, "E27.0.6.19", {"start": v(-105.88, 265) * mm, "end": v(-105.88, 256.18) * mm});
            skLineSegment(sketch, "E27.0.6.20", {"start": v(-70.59, 256.18) * mm, "end": v(-61.76, 256.18) * mm});
            skLineSegment(sketch, "E27.0.6.21", {"start": v(-35.3, 265) * mm, "end": v(-35.3, 256.18) * mm});
            skLineSegment(sketch, "E27.0.6.22", {"start": v(-114.7, 265) * mm, "end": v(-114.7, 256.18) * mm});
            skLineSegment(sketch, "E27.0.6.23", {"start": v(-44.12, 265) * mm, "end": v(-44.12, 256.18) * mm});
            skLineSegment(sketch, "E27.0.6.24", {"start": v(-79.41, 265) * mm, "end": v(-79.41, 256.18) * mm});
            skLineSegment(sketch, "E27.0.6.25", {"start": v(-8.82, 265) * mm, "end": v(-8.82, 256.18) * mm});
            skLineSegment(sketch, "E27.0.6.26", {"start": v(-123.53, 265) * mm, "end": v(-123.53, 256.18) * mm});
            skLineSegment(sketch, "E27.0.6.27", {"start": v(-52.94, 265) * mm, "end": v(-52.94, 256.18) * mm});
            skLineSegment(sketch, "E27.0.6.28", {"start": v(-114.7, 265) * mm, "end": v(-123.53, 265) * mm});
            skLineSegment(sketch, "E27.0.6.29", {"start": v(-70.59, 265) * mm, "end": v(-61.76, 265) * mm});
            skLineSegment(sketch, "E27.0.6.30", {"start": v(-8.82, 265) * mm, "end": v(-17.65, 265) * mm});
            skLineSegment(sketch, "E27.0.6.31", {"start": v(-88.24, 256.18) * mm, "end": v(-79.41, 256.18) * mm});
            skLineSegment(sketch, "E27.0.6.32", {"start": v(-35.3, 240) * mm, "end": v(-39.3, 240) * mm});
            skLineSegment(sketch, "E27.0.6.33", {"start": v(0, 265) * mm, "end": v(-8.82, 265) * mm});
            skLineSegment(sketch, "E27.0.6.34", {"start": v(-35.3, 244) * mm, "end": v(-39.3, 244) * mm});
            skLineSegment(sketch, "E27.0.6.35", {"start": v(-52.94, 256.18) * mm, "end": v(-44.12, 256.18) * mm});
            skLineSegment(sketch, "E27.0.6.36", {"start": v(-110.7, 240) * mm, "end": v(-110.7, 244) * mm});
            skLineSegment(sketch, "E27.0.6.37", {"start": v(-114.7, 240) * mm, "end": v(-114.7, 244) * mm});
            skLineSegment(sketch, "E27.0.6.38", {"start": v(-114.7, 244) * mm, "end": v(-110.7, 244) * mm});
            skLineSegment(sketch, "E27.0.6.39", {"start": v(-141.18, 256.18) * mm, "end": v(-132.35, 256.18) * mm});
            skLineSegment(sketch, "E27.0.6.40", {"start": v(-105.88, 256.18) * mm, "end": v(-97.06, 256.18) * mm});
            skLineSegment(sketch, "E27.0.6.41", {"start": v(-114.7, 240) * mm, "end": v(-110.7, 240) * mm});
            skLineSegment(sketch, "E27.0.6.42", {"start": v(-35.3, 256.18) * mm, "end": v(-26.47, 256.18) * mm});
            skLineSegment(sketch, "E27.0.6.43", {"start": v(-39.3, 240) * mm, "end": v(-39.3, 244) * mm});
            skLineSegment(sketch, "E27.0.6.44", {"start": v(-35.3, 240) * mm, "end": v(-35.3, 244) * mm});
            skLineSegment(sketch, "E27.0.6.45", {"start": v(-105.88, 265) * mm, "end": v(-114.7, 265) * mm});
            skLineSegment(sketch, "E27.0.6.46", {"start": v(-123.53, 265) * mm, "end": v(-132.35, 265) * mm});
            skLineSegment(sketch, "E27.0.6.47", {"start": v(-26.47, 265) * mm, "end": v(-35.3, 265) * mm});
            skLineSegment(sketch, "E27.0.6.48", {"start": v(-88.24, 265) * mm, "end": v(-79.41, 265) * mm});
            skLineSegment(sketch, "E27.0.6.49", {"start": v(-52.94, 265) * mm, "end": v(-44.12, 265) * mm});
            skLineSegment(sketch, "E27.0.6.50", {"start": v(-17.65, 265) * mm, "end": v(-26.47, 265) * mm});
            skLineSegment(sketch, "E27.0.6.51", {"start": v(-132.35, 265) * mm, "end": v(-141.18, 265) * mm});
            skLineSegment(sketch, "E27.0.6.52", {"start": v(-97.06, 265) * mm, "end": v(-105.88, 265) * mm});
            skLineSegment(sketch, "E27.0.6.53", {"start": v(-70.59, 265) * mm, "end": v(-79.41, 265) * mm});
            skLineSegment(sketch, "E27.0.6.54", {"start": v(-52.94, 265) * mm, "end": v(-61.76, 265) * mm});
            skLineSegment(sketch, "E27.0.6.55", {"start": v(-79.41, 265) * mm, "end": v(-88.24, 265) * mm});
            skLineSegment(sketch, "E27.0.6.56", {"start": v(-44.12, 265) * mm, "end": v(-52.94, 265) * mm});
            skLineSegment(sketch, "E27.0.6.57", {"start": v(-105.88, 265) * mm, "end": v(-97.06, 265) * mm});
            skLineSegment(sketch, "E27.0.6.58", {"start": v(-35.3, 265) * mm, "end": v(-26.47, 265) * mm});
            skLineSegment(sketch, "E27.0.6.59", {"start": v(-141.18, 265) * mm, "end": v(-132.35, 265) * mm});
            skLineSegment(sketch, "E27.0.7.0", {"start": v(-35.3, 305) * mm, "end": v(-44.12, 305) * mm});
            skLineSegment(sketch, "E27.0.7.1", {"start": v(-17.65, 296.18) * mm, "end": v(-8.82, 296.18) * mm});
            skLineSegment(sketch, "E27.0.7.2", {"start": v(-17.65, 305) * mm, "end": v(-17.65, 296.18) * mm});
            skLineSegment(sketch, "E27.0.7.3", {"start": v(-123.53, 305) * mm, "end": v(-114.7, 305) * mm});
            skLineSegment(sketch, "E27.0.7.4", {"start": v(-132.35, 305) * mm, "end": v(-132.35, 296.18) * mm});
            skLineSegment(sketch, "E27.0.7.5", {"start": v(-150, 280) * mm, "end": v(-150, 305) * mm});
            skLineSegment(sketch, "E27.0.7.6", {"start": v(0, 280) * mm, "end": v(0, 305) * mm});
            skLineSegment(sketch, "E27.0.7.7", {"start": v(-17.65, 305) * mm, "end": v(-8.82, 305) * mm});
            skLineSegment(sketch, "E27.0.7.8", {"start": v(-88.24, 305) * mm, "end": v(-97.06, 305) * mm});
            skLineSegment(sketch, "E27.0.7.9", {"start": v(-141.18, 305) * mm, "end": v(-150, 305) * mm});
            skLineSegment(sketch, "E27.0.7.10", {"start": v(-123.53, 296.18) * mm, "end": v(-114.7, 296.18) * mm});
            skLineSegment(sketch, "E27.0.7.11", {"start": v(0, 280) * mm, "end": v(-150, 280) * mm});
            skLineSegment(sketch, "E27.0.7.12", {"start": v(-61.76, 305) * mm, "end": v(-61.76, 296.18) * mm});
            skLineSegment(sketch, "E27.0.7.13", {"start": v(-88.24, 305) * mm, "end": v(-88.24, 296.18) * mm});
            skLineSegment(sketch, "E27.0.7.14", {"start": v(-61.76, 305) * mm, "end": v(-70.59, 305) * mm});
            skLineSegment(sketch, "E27.0.7.15", {"start": v(-70.59, 305) * mm, "end": v(-70.59, 296.18) * mm});
            skLineSegment(sketch, "E27.0.7.16", {"start": v(-97.06, 305) * mm, "end": v(-97.06, 296.18) * mm});
            skLineSegment(sketch, "E27.0.7.17", {"start": v(-26.47, 305) * mm, "end": v(-26.47, 296.18) * mm});
            skLineSegment(sketch, "E27.0.7.18", {"start": v(-141.18, 305) * mm, "end": v(-141.18, 296.18) * mm});
            skLineSegment(sketch, "E27.0.7.19", {"start": v(-105.88, 305) * mm, "end": v(-105.88, 296.18) * mm});
            skLineSegment(sketch, "E27.0.7.20", {"start": v(-70.59, 296.18) * mm, "end": v(-61.76, 296.18) * mm});
            skLineSegment(sketch, "E27.0.7.21", {"start": v(-35.3, 305) * mm, "end": v(-35.3, 296.18) * mm});
            skLineSegment(sketch, "E27.0.7.22", {"start": v(-114.7, 305) * mm, "end": v(-114.7, 296.18) * mm});
            skLineSegment(sketch, "E27.0.7.23", {"start": v(-44.12, 305) * mm, "end": v(-44.12, 296.18) * mm});
            skLineSegment(sketch, "E27.0.7.24", {"start": v(-79.41, 305) * mm, "end": v(-79.41, 296.18) * mm});
            skLineSegment(sketch, "E27.0.7.25", {"start": v(-8.82, 305) * mm, "end": v(-8.82, 296.18) * mm});
            skLineSegment(sketch, "E27.0.7.26", {"start": v(-123.53, 305) * mm, "end": v(-123.53, 296.18) * mm});
            skLineSegment(sketch, "E27.0.7.27", {"start": v(-52.94, 305) * mm, "end": v(-52.94, 296.18) * mm});
            skLineSegment(sketch, "E27.0.7.28", {"start": v(-114.7, 305) * mm, "end": v(-123.53, 305) * mm});
            skLineSegment(sketch, "E27.0.7.29", {"start": v(-70.59, 305) * mm, "end": v(-61.76, 305) * mm});
            skLineSegment(sketch, "E27.0.7.30", {"start": v(-8.82, 305) * mm, "end": v(-17.65, 305) * mm});
            skLineSegment(sketch, "E27.0.7.31", {"start": v(-88.24, 296.18) * mm, "end": v(-79.41, 296.18) * mm});
            skLineSegment(sketch, "E27.0.7.32", {"start": v(-35.3, 280) * mm, "end": v(-39.3, 280) * mm});
            skLineSegment(sketch, "E27.0.7.33", {"start": v(0, 305) * mm, "end": v(-8.82, 305) * mm});
            skLineSegment(sketch, "E27.0.7.34", {"start": v(-35.3, 284) * mm, "end": v(-39.3, 284) * mm});
            skLineSegment(sketch, "E27.0.7.35", {"start": v(-52.94, 296.18) * mm, "end": v(-44.12, 296.18) * mm});
            skLineSegment(sketch, "E27.0.7.36", {"start": v(-110.7, 280) * mm, "end": v(-110.7, 284) * mm});
            skLineSegment(sketch, "E27.0.7.37", {"start": v(-114.7, 280) * mm, "end": v(-114.7, 284) * mm});
            skLineSegment(sketch, "E27.0.7.38", {"start": v(-114.7, 284) * mm, "end": v(-110.7, 284) * mm});
            skLineSegment(sketch, "E27.0.7.39", {"start": v(-141.18, 296.18) * mm, "end": v(-132.35, 296.18) * mm});
            skLineSegment(sketch, "E27.0.7.40", {"start": v(-105.88, 296.18) * mm, "end": v(-97.06, 296.18) * mm});
            skLineSegment(sketch, "E27.0.7.41", {"start": v(-114.7, 280) * mm, "end": v(-110.7, 280) * mm});
            skLineSegment(sketch, "E27.0.7.42", {"start": v(-35.3, 296.18) * mm, "end": v(-26.47, 296.18) * mm});
            skLineSegment(sketch, "E27.0.7.43", {"start": v(-39.3, 280) * mm, "end": v(-39.3, 284) * mm});
            skLineSegment(sketch, "E27.0.7.44", {"start": v(-35.3, 280) * mm, "end": v(-35.3, 284) * mm});
            skLineSegment(sketch, "E27.0.7.45", {"start": v(-105.88, 305) * mm, "end": v(-114.7, 305) * mm});
            skLineSegment(sketch, "E27.0.7.46", {"start": v(-123.53, 305) * mm, "end": v(-132.35, 305) * mm});
            skLineSegment(sketch, "E27.0.7.47", {"start": v(-26.47, 305) * mm, "end": v(-35.3, 305) * mm});
            skLineSegment(sketch, "E27.0.7.48", {"start": v(-88.24, 305) * mm, "end": v(-79.41, 305) * mm});
            skLineSegment(sketch, "E27.0.7.49", {"start": v(-52.94, 305) * mm, "end": v(-44.12, 305) * mm});
            skLineSegment(sketch, "E27.0.7.50", {"start": v(-17.65, 305) * mm, "end": v(-26.47, 305) * mm});
            skLineSegment(sketch, "E27.0.7.51", {"start": v(-132.35, 305) * mm, "end": v(-141.18, 305) * mm});
            skLineSegment(sketch, "E27.0.7.52", {"start": v(-97.06, 305) * mm, "end": v(-105.88, 305) * mm});
            skLineSegment(sketch, "E27.0.7.53", {"start": v(-70.59, 305) * mm, "end": v(-79.41, 305) * mm});
            skLineSegment(sketch, "E27.0.7.54", {"start": v(-52.94, 305) * mm, "end": v(-61.76, 305) * mm});
            skLineSegment(sketch, "E27.0.7.55", {"start": v(-79.41, 305) * mm, "end": v(-88.24, 305) * mm});
            skLineSegment(sketch, "E27.0.7.56", {"start": v(-44.12, 305) * mm, "end": v(-52.94, 305) * mm});
            skLineSegment(sketch, "E27.0.7.57", {"start": v(-105.88, 305) * mm, "end": v(-97.06, 305) * mm});
            skLineSegment(sketch, "E27.0.7.58", {"start": v(-35.3, 305) * mm, "end": v(-26.47, 305) * mm});
            skLineSegment(sketch, "E27.0.7.59", {"start": v(-141.18, 305) * mm, "end": v(-132.35, 305) * mm});
            skLineSegment(sketch, "E27.0.8.0", {"start": v(-35.3, 345) * mm, "end": v(-44.12, 345) * mm});
            skLineSegment(sketch, "E27.0.8.1", {"start": v(-17.65, 336.18) * mm, "end": v(-8.82, 336.18) * mm});
            skLineSegment(sketch, "E27.0.8.2", {"start": v(-17.65, 345) * mm, "end": v(-17.65, 336.18) * mm});
            skLineSegment(sketch, "E27.0.8.3", {"start": v(-123.53, 345) * mm, "end": v(-114.7, 345) * mm});
            skLineSegment(sketch, "E27.0.8.4", {"start": v(-132.35, 345) * mm, "end": v(-132.35, 336.18) * mm});
            skLineSegment(sketch, "E27.0.8.5", {"start": v(-150, 320) * mm, "end": v(-150, 345) * mm});
            skLineSegment(sketch, "E27.0.8.6", {"start": v(0, 320) * mm, "end": v(0, 345) * mm});
            skLineSegment(sketch, "E27.0.8.7", {"start": v(-17.65, 345) * mm, "end": v(-8.82, 345) * mm});
            skLineSegment(sketch, "E27.0.8.8", {"start": v(-88.24, 345) * mm, "end": v(-97.06, 345) * mm});
            skLineSegment(sketch, "E27.0.8.9", {"start": v(-141.18, 345) * mm, "end": v(-150, 345) * mm});
            skLineSegment(sketch, "E27.0.8.10", {"start": v(-123.53, 336.18) * mm, "end": v(-114.7, 336.18) * mm});
            skLineSegment(sketch, "E27.0.8.11", {"start": v(0, 320) * mm, "end": v(-150, 320) * mm});
            skLineSegment(sketch, "E27.0.8.12", {"start": v(-61.76, 345) * mm, "end": v(-61.76, 336.18) * mm});
            skLineSegment(sketch, "E27.0.8.13", {"start": v(-88.24, 345) * mm, "end": v(-88.24, 336.18) * mm});
            skLineSegment(sketch, "E27.0.8.14", {"start": v(-61.76, 345) * mm, "end": v(-70.59, 345) * mm});
            skLineSegment(sketch, "E27.0.8.15", {"start": v(-70.59, 345) * mm, "end": v(-70.59, 336.18) * mm});
            skLineSegment(sketch, "E27.0.8.16", {"start": v(-97.06, 345) * mm, "end": v(-97.06, 336.18) * mm});
            skLineSegment(sketch, "E27.0.8.17", {"start": v(-26.47, 345) * mm, "end": v(-26.47, 336.18) * mm});
            skLineSegment(sketch, "E27.0.8.18", {"start": v(-141.18, 345) * mm, "end": v(-141.18, 336.18) * mm});
            skLineSegment(sketch, "E27.0.8.19", {"start": v(-105.88, 345) * mm, "end": v(-105.88, 336.18) * mm});
            skLineSegment(sketch, "E27.0.8.20", {"start": v(-70.59, 336.18) * mm, "end": v(-61.76, 336.18) * mm});
            skLineSegment(sketch, "E27.0.8.21", {"start": v(-35.3, 345) * mm, "end": v(-35.3, 336.18) * mm});
            skLineSegment(sketch, "E27.0.8.22", {"start": v(-114.7, 345) * mm, "end": v(-114.7, 336.18) * mm});
            skLineSegment(sketch, "E27.0.8.23", {"start": v(-44.12, 345) * mm, "end": v(-44.12, 336.18) * mm});
            skLineSegment(sketch, "E27.0.8.24", {"start": v(-79.41, 345) * mm, "end": v(-79.41, 336.18) * mm});
            skLineSegment(sketch, "E27.0.8.25", {"start": v(-8.82, 345) * mm, "end": v(-8.82, 336.18) * mm});
            skLineSegment(sketch, "E27.0.8.26", {"start": v(-123.53, 345) * mm, "end": v(-123.53, 336.18) * mm});
            skLineSegment(sketch, "E27.0.8.27", {"start": v(-52.94, 345) * mm, "end": v(-52.94, 336.18) * mm});
            skLineSegment(sketch, "E27.0.8.28", {"start": v(-114.7, 345) * mm, "end": v(-123.53, 345) * mm});
            skLineSegment(sketch, "E27.0.8.29", {"start": v(-70.59, 345) * mm, "end": v(-61.76, 345) * mm});
            skLineSegment(sketch, "E27.0.8.30", {"start": v(-8.82, 345) * mm, "end": v(-17.65, 345) * mm});
            skLineSegment(sketch, "E27.0.8.31", {"start": v(-88.24, 336.18) * mm, "end": v(-79.41, 336.18) * mm});
            skLineSegment(sketch, "E27.0.8.32", {"start": v(-35.3, 320) * mm, "end": v(-39.3, 320) * mm});
            skLineSegment(sketch, "E27.0.8.33", {"start": v(0, 345) * mm, "end": v(-8.82, 345) * mm});
            skLineSegment(sketch, "E27.0.8.34", {"start": v(-35.3, 324) * mm, "end": v(-39.3, 324) * mm});
            skLineSegment(sketch, "E27.0.8.35", {"start": v(-52.94, 336.18) * mm, "end": v(-44.12, 336.18) * mm});
            skLineSegment(sketch, "E27.0.8.36", {"start": v(-110.7, 320) * mm, "end": v(-110.7, 324) * mm});
            skLineSegment(sketch, "E27.0.8.37", {"start": v(-114.7, 320) * mm, "end": v(-114.7, 324) * mm});
            skLineSegment(sketch, "E27.0.8.38", {"start": v(-114.7, 324) * mm, "end": v(-110.7, 324) * mm});
            skLineSegment(sketch, "E27.0.8.39", {"start": v(-141.18, 336.18) * mm, "end": v(-132.35, 336.18) * mm});
            skLineSegment(sketch, "E27.0.8.40", {"start": v(-105.88, 336.18) * mm, "end": v(-97.06, 336.18) * mm});
            skLineSegment(sketch, "E27.0.8.41", {"start": v(-114.7, 320) * mm, "end": v(-110.7, 320) * mm});
            skLineSegment(sketch, "E27.0.8.42", {"start": v(-35.3, 336.18) * mm, "end": v(-26.47, 336.18) * mm});
            skLineSegment(sketch, "E27.0.8.43", {"start": v(-39.3, 320) * mm, "end": v(-39.3, 324) * mm});
            skLineSegment(sketch, "E27.0.8.44", {"start": v(-35.3, 320) * mm, "end": v(-35.3, 324) * mm});
            skLineSegment(sketch, "E27.0.8.45", {"start": v(-105.88, 345) * mm, "end": v(-114.7, 345) * mm});
            skLineSegment(sketch, "E27.0.8.46", {"start": v(-123.53, 345) * mm, "end": v(-132.35, 345) * mm});
            skLineSegment(sketch, "E27.0.8.47", {"start": v(-26.47, 345) * mm, "end": v(-35.3, 345) * mm});
            skLineSegment(sketch, "E27.0.8.48", {"start": v(-88.24, 345) * mm, "end": v(-79.41, 345) * mm});
            skLineSegment(sketch, "E27.0.8.49", {"start": v(-52.94, 345) * mm, "end": v(-44.12, 345) * mm});
            skLineSegment(sketch, "E27.0.8.50", {"start": v(-17.65, 345) * mm, "end": v(-26.47, 345) * mm});
            skLineSegment(sketch, "E27.0.8.51", {"start": v(-132.35, 345) * mm, "end": v(-141.18, 345) * mm});
            skLineSegment(sketch, "E27.0.8.52", {"start": v(-97.06, 345) * mm, "end": v(-105.88, 345) * mm});
            skLineSegment(sketch, "E27.0.8.53", {"start": v(-70.59, 345) * mm, "end": v(-79.41, 345) * mm});
            skLineSegment(sketch, "E27.0.8.54", {"start": v(-52.94, 345) * mm, "end": v(-61.76, 345) * mm});
            skLineSegment(sketch, "E27.0.8.55", {"start": v(-79.41, 345) * mm, "end": v(-88.24, 345) * mm});
            skLineSegment(sketch, "E27.0.8.56", {"start": v(-44.12, 345) * mm, "end": v(-52.94, 345) * mm});
            skLineSegment(sketch, "E27.0.8.57", {"start": v(-105.88, 345) * mm, "end": v(-97.06, 345) * mm});
            skLineSegment(sketch, "E27.0.8.58", {"start": v(-35.3, 345) * mm, "end": v(-26.47, 345) * mm});
            skLineSegment(sketch, "E27.0.8.59", {"start": v(-141.18, 345) * mm, "end": v(-132.35, 345) * mm});
            skLineSegment(sketch, "E27.0.9.0", {"start": v(-35.3, 385) * mm, "end": v(-44.12, 385) * mm});
            skLineSegment(sketch, "E27.0.9.1", {"start": v(-17.65, 376.18) * mm, "end": v(-8.82, 376.18) * mm});
            skLineSegment(sketch, "E27.0.9.2", {"start": v(-17.65, 385) * mm, "end": v(-17.65, 376.18) * mm});
            skLineSegment(sketch, "E27.0.9.3", {"start": v(-123.53, 385) * mm, "end": v(-114.7, 385) * mm});
            skLineSegment(sketch, "E27.0.9.4", {"start": v(-132.35, 385) * mm, "end": v(-132.35, 376.18) * mm});
            skLineSegment(sketch, "E27.0.9.5", {"start": v(-150, 360) * mm, "end": v(-150, 385) * mm});
            skLineSegment(sketch, "E27.0.9.6", {"start": v(0, 360) * mm, "end": v(0, 385) * mm});
            skLineSegment(sketch, "E27.0.9.7", {"start": v(-17.65, 385) * mm, "end": v(-8.82, 385) * mm});
            skLineSegment(sketch, "E27.0.9.8", {"start": v(-88.24, 385) * mm, "end": v(-97.06, 385) * mm});
            skLineSegment(sketch, "E27.0.9.9", {"start": v(-141.18, 385) * mm, "end": v(-150, 385) * mm});
            skLineSegment(sketch, "E27.0.9.10", {"start": v(-123.53, 376.18) * mm, "end": v(-114.7, 376.18) * mm});
            skLineSegment(sketch, "E27.0.9.11", {"start": v(0, 360) * mm, "end": v(-150, 360) * mm});
            skLineSegment(sketch, "E27.0.9.12", {"start": v(-61.76, 385) * mm, "end": v(-61.76, 376.18) * mm});
            skLineSegment(sketch, "E27.0.9.13", {"start": v(-88.24, 385) * mm, "end": v(-88.24, 376.18) * mm});
            skLineSegment(sketch, "E27.0.9.14", {"start": v(-61.76, 385) * mm, "end": v(-70.59, 385) * mm});
            skLineSegment(sketch, "E27.0.9.15", {"start": v(-70.59, 385) * mm, "end": v(-70.59, 376.18) * mm});
            skLineSegment(sketch, "E27.0.9.16", {"start": v(-97.06, 385) * mm, "end": v(-97.06, 376.18) * mm});
            skLineSegment(sketch, "E27.0.9.17", {"start": v(-26.47, 385) * mm, "end": v(-26.47, 376.18) * mm});
            skLineSegment(sketch, "E27.0.9.18", {"start": v(-141.18, 385) * mm, "end": v(-141.18, 376.18) * mm});
            skLineSegment(sketch, "E27.0.9.19", {"start": v(-105.88, 385) * mm, "end": v(-105.88, 376.18) * mm});
            skLineSegment(sketch, "E27.0.9.20", {"start": v(-70.59, 376.18) * mm, "end": v(-61.76, 376.18) * mm});
            skLineSegment(sketch, "E27.0.9.21", {"start": v(-35.3, 385) * mm, "end": v(-35.3, 376.18) * mm});
            skLineSegment(sketch, "E27.0.9.22", {"start": v(-114.7, 385) * mm, "end": v(-114.7, 376.18) * mm});
            skLineSegment(sketch, "E27.0.9.23", {"start": v(-44.12, 385) * mm, "end": v(-44.12, 376.18) * mm});
            skLineSegment(sketch, "E27.0.9.24", {"start": v(-79.41, 385) * mm, "end": v(-79.41, 376.18) * mm});
            skLineSegment(sketch, "E27.0.9.25", {"start": v(-8.82, 385) * mm, "end": v(-8.82, 376.18) * mm});
            skLineSegment(sketch, "E27.0.9.26", {"start": v(-123.53, 385) * mm, "end": v(-123.53, 376.18) * mm});
            skLineSegment(sketch, "E27.0.9.27", {"start": v(-52.94, 385) * mm, "end": v(-52.94, 376.18) * mm});
            skLineSegment(sketch, "E27.0.9.28", {"start": v(-114.7, 385) * mm, "end": v(-123.53, 385) * mm});
            skLineSegment(sketch, "E27.0.9.29", {"start": v(-70.59, 385) * mm, "end": v(-61.76, 385) * mm});
            skLineSegment(sketch, "E27.0.9.30", {"start": v(-8.82, 385) * mm, "end": v(-17.65, 385) * mm});
            skLineSegment(sketch, "E27.0.9.31", {"start": v(-88.24, 376.18) * mm, "end": v(-79.41, 376.18) * mm});
            skLineSegment(sketch, "E27.0.9.32", {"start": v(-35.3, 360) * mm, "end": v(-39.3, 360) * mm});
            skLineSegment(sketch, "E27.0.9.33", {"start": v(0, 385) * mm, "end": v(-8.82, 385) * mm});
            skLineSegment(sketch, "E27.0.9.34", {"start": v(-35.3, 364) * mm, "end": v(-39.3, 364) * mm});
            skLineSegment(sketch, "E27.0.9.35", {"start": v(-52.94, 376.18) * mm, "end": v(-44.12, 376.18) * mm});
            skLineSegment(sketch, "E27.0.9.36", {"start": v(-110.7, 360) * mm, "end": v(-110.7, 364) * mm});
            skLineSegment(sketch, "E27.0.9.37", {"start": v(-114.7, 360) * mm, "end": v(-114.7, 364) * mm});
            skLineSegment(sketch, "E27.0.9.38", {"start": v(-114.7, 364) * mm, "end": v(-110.7, 364) * mm});
            skLineSegment(sketch, "E27.0.9.39", {"start": v(-141.18, 376.18) * mm, "end": v(-132.35, 376.18) * mm});
            skLineSegment(sketch, "E27.0.9.40", {"start": v(-105.88, 376.18) * mm, "end": v(-97.06, 376.18) * mm});
            skLineSegment(sketch, "E27.0.9.41", {"start": v(-114.7, 360) * mm, "end": v(-110.7, 360) * mm});
            skLineSegment(sketch, "E27.0.9.42", {"start": v(-35.3, 376.18) * mm, "end": v(-26.47, 376.18) * mm});
            skLineSegment(sketch, "E27.0.9.43", {"start": v(-39.3, 360) * mm, "end": v(-39.3, 364) * mm});
            skLineSegment(sketch, "E27.0.9.44", {"start": v(-35.3, 360) * mm, "end": v(-35.3, 364) * mm});
            skLineSegment(sketch, "E27.0.9.45", {"start": v(-105.88, 385) * mm, "end": v(-114.7, 385) * mm});
            skLineSegment(sketch, "E27.0.9.46", {"start": v(-123.53, 385) * mm, "end": v(-132.35, 385) * mm});
            skLineSegment(sketch, "E27.0.9.47", {"start": v(-26.47, 385) * mm, "end": v(-35.3, 385) * mm});
            skLineSegment(sketch, "E27.0.9.48", {"start": v(-88.24, 385) * mm, "end": v(-79.41, 385) * mm});
            skLineSegment(sketch, "E27.0.9.49", {"start": v(-52.94, 385) * mm, "end": v(-44.12, 385) * mm});
            skLineSegment(sketch, "E27.0.9.50", {"start": v(-17.65, 385) * mm, "end": v(-26.47, 385) * mm});
            skLineSegment(sketch, "E27.0.9.51", {"start": v(-132.35, 385) * mm, "end": v(-141.18, 385) * mm});
            skLineSegment(sketch, "E27.0.9.52", {"start": v(-97.06, 385) * mm, "end": v(-105.88, 385) * mm});
            skLineSegment(sketch, "E27.0.9.53", {"start": v(-70.59, 385) * mm, "end": v(-79.41, 385) * mm});
            skLineSegment(sketch, "E27.0.9.54", {"start": v(-52.94, 385) * mm, "end": v(-61.76, 385) * mm});
            skLineSegment(sketch, "E27.0.9.55", {"start": v(-79.41, 385) * mm, "end": v(-88.24, 385) * mm});
            skLineSegment(sketch, "E27.0.9.56", {"start": v(-44.12, 385) * mm, "end": v(-52.94, 385) * mm});
            skLineSegment(sketch, "E27.0.9.57", {"start": v(-105.88, 385) * mm, "end": v(-97.06, 385) * mm});
            skLineSegment(sketch, "E27.0.9.58", {"start": v(-35.3, 385) * mm, "end": v(-26.47, 385) * mm});
            skLineSegment(sketch, "E27.0.9.59", {"start": v(-141.18, 385) * mm, "end": v(-132.35, 385) * mm});
            skLineSegment(sketch, "E27.direction1", {"start": v(-150, 0) * mm, "end": v(-103, 0) * mm, "construction": true});
            skLineSegment(sketch, "E27.direction2", {"start": v(-150, 0) * mm, "end": v(-150, 40) * mm, "construction": true});
            skSolve(sketch);
        }
        {
            var Q0;
            Q0=makeQuery(id+"F0.imprint","IMPRINT",FACE,{"disambiguationData":[TD([[makeQuery(id+"F0.imprint","IMPRINT",EDGE,{"derivedFrom":sQuery(id+"F0.wireOp",EDGE,"E0.top")}),1.0]])]});
            extrude(context, id + "F1", {"entities" : qUnion([Q0]), "oppositeDirection" : true, "depth" : 3000 * mm});
        }
        {
            var Q0;
            Q0=makeQuery(id+"F0.imprint","IMPRINT",FACE,{"disambiguationData":[TD([[makeQuery(id+"F0.imprint","IMPRINT",EDGE,{"derivedFrom":sQuery(id+"F0.wireOp",EDGE,"E27.0.1.0")}),1.0]])]});
            extrude(context, id + "F2", {"entities" : qUnion([Q0]), "oppositeDirection" : true, "depth" : 2000 * mm});
        }
        {
            var Q0;
            Q0=makeQuery(id+"F0.imprint","IMPRINT",FACE,{"disambiguationData":[TD([[makeQuery(id+"F0.imprint","IMPRINT",EDGE,{"derivedFrom":sQuery(id+"F0.wireOp",EDGE,"E27.0.2.0")}),1.0]])]});
            extrude(context, id + "F3", {"entities" : qUnion([Q0]), "oppositeDirection" : true, "depth" : (2 - (4 * 0.03)) * mm});
        }
        {
            var Q0;
            Q0=makeQuery(id+"F0.imprint","IMPRINT",FACE,{"disambiguationData":[TD([[makeQuery(id+"F0.imprint","IMPRINT",EDGE,{"derivedFrom":sQuery(id+"F0.wireOp",EDGE,"E27.0.3.0")}),1.0]])]});
            extrude(context, id + "F4", {"entities" : qUnion([Q0]), "oppositeDirection" : true, "depth" : 900 * mm});
        }
        {
            var Q0;
            Q0=makeQuery(id+"F0.imprint","IMPRINT",FACE,{"disambiguationData":[TD([[makeQuery(id+"F0.imprint","IMPRINT",EDGE,{"derivedFrom":sQuery(id+"F0.wireOp",EDGE,"E27.0.4.0")}),1.0]])]});
            extrude(context, id + "F5", {"entities" : qUnion([Q0]), "oppositeDirection" : true, "depth" : 600 * mm});
        }
        {
            var Q0;
            Q0=makeQuery(id+"F0.imprint","IMPRINT",FACE,{"disambiguationData":[TD([[makeQuery(id+"F0.imprint","IMPRINT",EDGE,{"derivedFrom":sQuery(id+"F0.wireOp",EDGE,"E27.0.5.0")}),1.0]])]});
            extrude(context, id + "F6", {"entities" : qUnion([Q0]), "oppositeDirection" : true, "depth" : 500 * mm});
        }
    });
